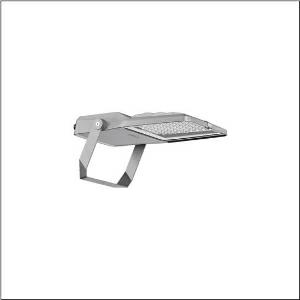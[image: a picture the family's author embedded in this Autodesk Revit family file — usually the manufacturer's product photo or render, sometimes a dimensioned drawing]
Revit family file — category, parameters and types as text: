
# Revit family: floodlight_fl_21_mini___pl61_5xa7775c2c1a_7daf
name_source: partatom
category: Lighting Fixtures
units: mm (PartAtom-declared; Revit-internal decimal feet)

## family parameters
Cut with Voids When Loaded = No
Host = Face
Light Source = No
Part Type = Normal
Room Calculation Point = No
Round Connector Dimension = Use Diameter
Shared = No

## types (1)
- --- (1 x LED, 11960 lm, 89 W, 3000K)
    Apparent Load = 89 VA
    CIE Flux Codes = 33 65 98 100 100
    Color Rendering = 70
    Color Temperature = 3000K
    Default Elevation = 1800 mm
    Description = Floodlight FL 21 mini, floodlight, primary light control with lens, of PMMA, primary optical cover: protective disc, of toughened safety glass, transparent, light distribution: PL61, light emission: direct distribution, installation type: surface-mounted, LED, High Power LED, rated luminous flux: 11.960lm, luminous efficacy: 134lm/W, light colour: 730, colour temperature: 3000K, control gear: Smart Interface (Zhaga), control: flexible luminous flux parameterisation, time-dependent luminous flux control, constant luminous flux control, overheat protection, pre-setting: logarithmic dimming characteristic, with terminal, 6-pole, mains connection: 220..240V, AC, 50/60Hz, start of lifetime: 89W, end of service life: 94W, reduction: 43W, luminaire housing, of diecast aluminium, powder-coated, Siteco® metallic grey (DB 702S), corrosivity category C5 mid according to DIN EN ISO 12944, suitable for swimming pools, chlorine-resistant, sealing non-destructively replaceable, mounting bracket, of steel, galvanised, powder-coated, Siteco® metallic grey (DB 702S), Smart Interface above, protection rating (complete): IP66, insulation class (complete): insulation class II (safety insulation), certification: CE, ENEC, VDE, protection symbol: D, impact resistance: IK08, permissible operating ambient temperature: -40..+40°C, permissible operating ambient temperature for outdoor applications: -40..+50°C, standard: DIN EN 12944, LABS conformity tested according to VDMA 24364:2018-05, packaging unit: 1 piece

Light Distribution: PL61
    Height = 70 mm
    Lamp = 1 x LED
    Lamp Light Flux = 11960 lm
    Lamp Power = 89 W
    Lamp count = 1
    Length = 485 mm
    Luminous efficacy = 134 lm/W
    Manufacturer = Siteco
    ModVariant = No
    Model = 5XA7775C2C1A
    Number of Poles = 1
    OnlyDefault = Yes
    Power Factor = 1
    Product Name = Floodlight FL 21 mini | PL61
    Product group = floodlight | pylon annexe
    ProductGroupID = 6200
    Protection Class = Protection class II
    Protection Degree = IP 66
    RLX_Detail_Level = 1
    RLX_Emergency_Light_Flux = 0 lm
    RLX_Emergency_Type = 0
    RLX_Emergency_Type_DB = No
    RlxData = <blob elided: 95993 chars, md5=44e3525d>
    Socket = socket
    Standby Power = 0 W
    System Light Flux = 11960 lm
    System Power = 89 W
    Type Comments = factory setting: luminous flux: 100 % | dim-lin: 254 | 456 mA
    Type Image = l_1006845.jpg
    URL = http://relux.com
    VarID = @adj_172094
    Voltage = 0 V
    Weight = 0.00 kg
    Width = 337 mm

## geometry (parser evidence)
native form markers: Blend x4, Sweep x12
no freeform markers — native parametric forms only
